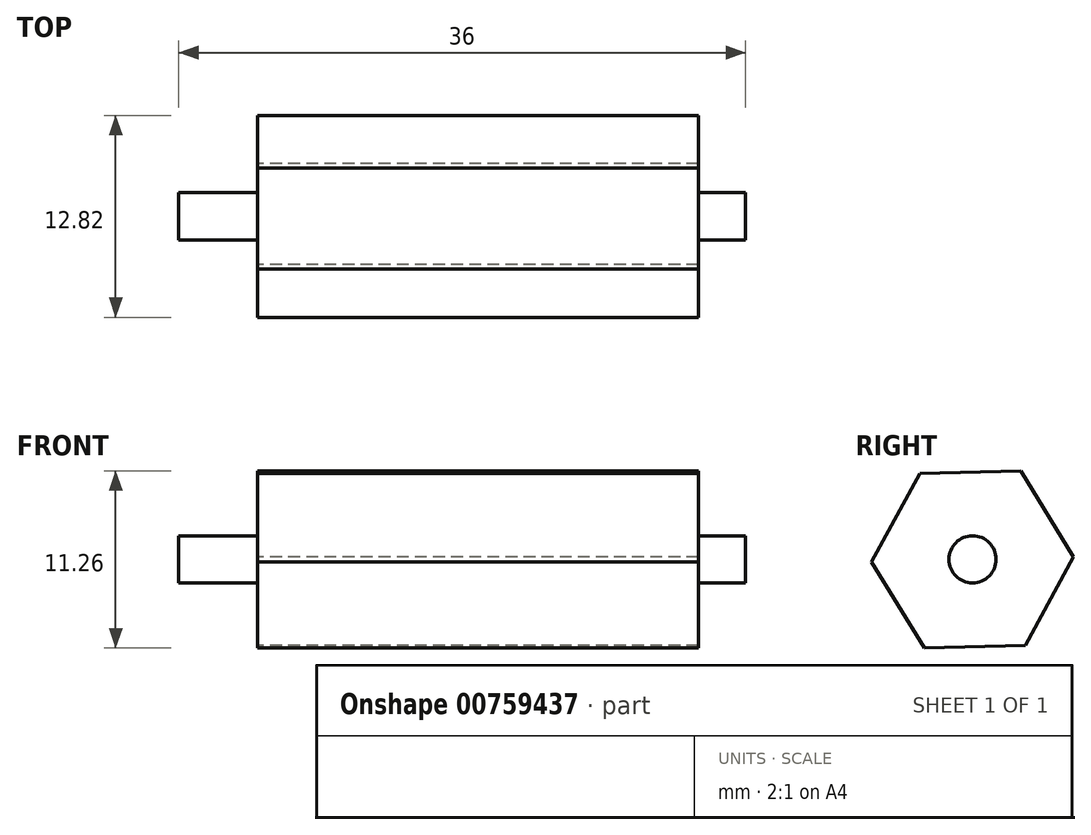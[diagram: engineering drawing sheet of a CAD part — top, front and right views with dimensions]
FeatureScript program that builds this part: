
annotation { "Feature Type Name" : "Feature", "Feature Type Description" : "" }
export const myFeature = defineFeature(function(context is Context, id is Id, definition is map)
    precondition{}
    {
        {
            var Q0;
            Q0=qCreatedBy(makeId("Right.planeOp"),FACE);
            var sketch = newSketch(context, id + "F0", { "sketchPlane" : qUnion([Q0])});
            skCircle(sketch, "E0.cCircle", {"center": v(0, 0) * mm, "radius": 5.55 * mm, "construction": true});
            skLineSegment(sketch, "E0.0", {"start": v(-6.41, -0.16) * mm, "end": v(-3.35, 5.47) * mm});
            skLineSegment(sketch, "E0.1", {"start": v(-3.35, 5.47) * mm, "end": v(3.07, 5.63) * mm});
            skLineSegment(sketch, "E0.2", {"start": v(3.07, 5.63) * mm, "end": v(6.41, 0.16) * mm});
            skLineSegment(sketch, "E0.3", {"start": v(6.41, 0.16) * mm, "end": v(3.35, -5.47) * mm});
            skLineSegment(sketch, "E0.4", {"start": v(3.35, -5.47) * mm, "end": v(-3.07, -5.63) * mm});
            skLineSegment(sketch, "E0.5", {"start": v(-3.07, -5.63) * mm, "end": v(-6.41, -0.16) * mm});
            skPoint(sketch, "E0.0.midPoint", {"position": v(-4.88, 2.66) * mm});
            skSolve(sketch);
        }
        {
            var Q0;
            Q0 = qSketchRegion(id + "F0", true);
            extrude(context, id + "F1", {"entities" : qUnion([Q0]), "endBound" : BoundingType.SYMMETRIC, "depth" : 28 * mm, "offsetDistance" : 25 * mm});
        }
        {
            var Q0;
            Q0=makeQuery(id+"F1.opExtrude","CAP_FACE",FACE,{"disambiguationData":[OSD([sQuery(id+"F0.wireOp",EDGE,"E0.0"),sQuery(id+"F0.wireOp",EDGE,"E0.1"),sQuery(id+"F0.wireOp",EDGE,"E0.2"),sQuery(id+"F0.wireOp",EDGE,"E0.3"),sQuery(id+"F0.wireOp",EDGE,"E0.4"),sQuery(id+"F0.wireOp",EDGE,"E0.5")])],"isStart":false});
            var sketch = newSketch(context, id + "F2", { "sketchPlane" : qUnion([Q0])});
            skCircle(sketch, "E1", {"center": v(0, 0) * mm, "radius": 1.5 * mm});
            skSolve(sketch);
        }
        {
            var Q0;
            Q0 = qSketchRegion(id + "F2", true);
            extrude(context, id + "F3", {"entities" : qUnion([Q0]), "operationType" : NewBodyOperationType.ADD, "depth" : 3 * mm, "offsetDistance" : 25 * mm});
        }
        {
            var Q0;
            Q0=makeQuery(id+"F1.opExtrude","CAP_FACE",FACE,{"disambiguationData":[OSD([sQuery(id+"F0.wireOp",EDGE,"E0.0"),sQuery(id+"F0.wireOp",EDGE,"E0.1"),sQuery(id+"F0.wireOp",EDGE,"E0.2"),sQuery(id+"F0.wireOp",EDGE,"E0.3"),sQuery(id+"F0.wireOp",EDGE,"E0.4"),sQuery(id+"F0.wireOp",EDGE,"E0.5")])],"isStart":true});
            var sketch = newSketch(context, id + "F4", { "sketchPlane" : qUnion([Q0])});
            skCircle(sketch, "E2", {"center": v(0, 0) * mm, "radius": 1.5 * mm});
            skSolve(sketch);
        }
        {
            var Q0;
            Q0 = qSketchRegion(id + "F4", true);
            extrude(context, id + "F5", {"entities" : qUnion([Q0]), "operationType" : NewBodyOperationType.ADD, "depth" : 5 * mm, "offsetDistance" : 25 * mm});
        }
    });
